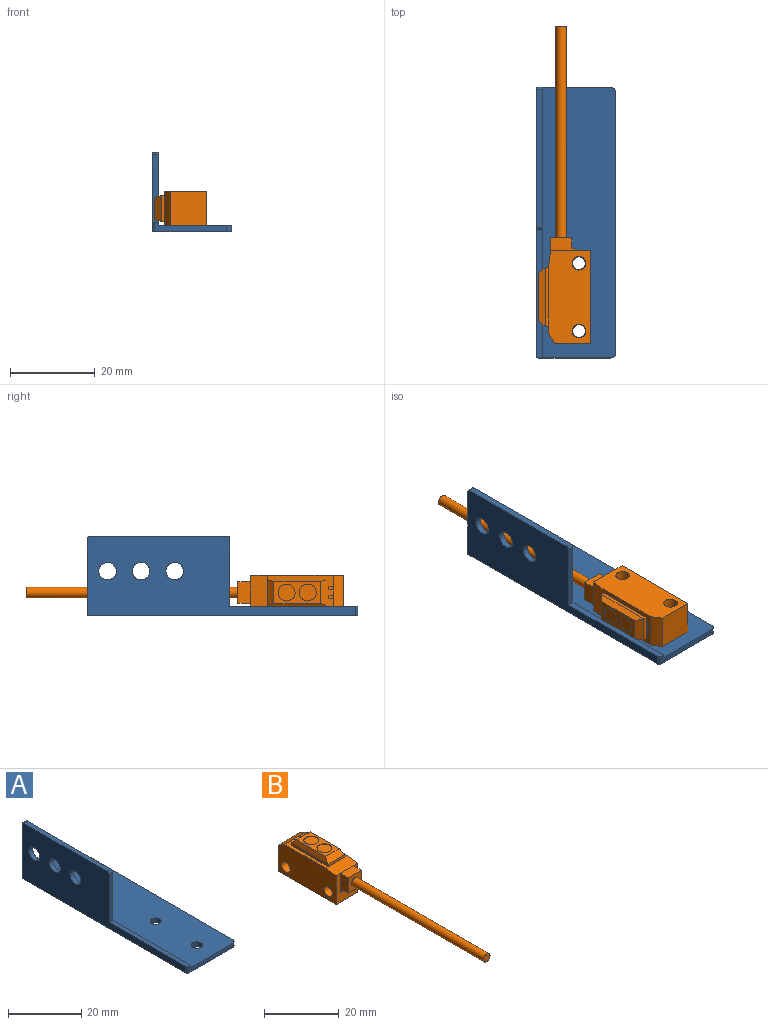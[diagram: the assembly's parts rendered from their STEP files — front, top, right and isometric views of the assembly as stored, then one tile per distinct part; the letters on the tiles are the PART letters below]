
ASSEMBLY  parts=2 mates=1
PART A: 20 faces, bbox 18.8x63.9x18.8 mm
  f0: plane 30.23x1.4mm, normal (0,0,1), area 42.1mm2, adj f3,f4,f9,f10,f16
  f1: plane 63.88x17.4mm, normal (0,0,1), area 1096.6mm2, adj f2,f4,f5,f6,f7,f9,f12,f13
  f2: plane 18.16x17.53mm, normal (0,1,0), area 47.9mm2, adj f1,f3,f8,f9,f13,f15
  f3: plane 63.25x18.8mm, normal (-1,0,0), area 655.4mm2, adj f0,f2,f8,f10,f11,f14,f15,f16
  f4: plane 16.89x2.16mm, normal (0,-1,0), area 24.2mm2, adj f0,f1,f8,f9,f12,f16
  f5: cylinder r=1.5mm len=3mm, axis (0,0,1), area 13.2mm2, adj f1,f8
  f6: plane 61.34x1.4mm, normal (1,0,0), area 85.7mm2, adj f1,f8,f12,f13
  f7: cylinder r=1.5mm len=3mm, axis (0,0,1), area 13.2mm2, adj f1,f8
  f8: plane 63.88x18.8mm, normal (0,0,-1), area 1185.8mm2, adj f2,f3,f4,f5,f6,f7,f12,f13
  f9: plane 63.88x17.4mm, normal (1,0,0), area 567.5mm2, adj f0,f1,f2,f4,f10,f11,f14,f15
  f10: plane 16x1.4mm, normal (0,-1,0), area 22.4mm2, adj f0,f3,f9,f14
  f11: plane 32.39x1.4mm, normal (0,0,1), area 45.2mm2, adj f3,f9,f14,f15
  f12: cylinder r=1.27mm len=1.4mm, axis (0,0,-1), area 2.8mm2, adj f1,f4,f6,f8
  f13: cylinder r=1.27mm len=1.4mm, axis (0,0,1), area 2.8mm2, adj f1,f2,f6,f8
  f14: cylinder r=0.64mm len=1.4mm, axis (-1,0,0), area 1.4mm2, adj f3,f9,f10,f11
  f15: cylinder r=0.64mm len=1.4mm, axis (-1,0,0), area 1.4mm2, adj f2,f3,f9,f11
  f16: cylinder r=0.64mm len=2.16mm, axis (0,0,1), area 2.2mm2, adj f0,f3,f4,f8
  f17: cylinder r=2.08mm len=4.17mm, axis (-1,0,0), area 18.3mm2, adj f3,f9
  f18: cylinder r=2.08mm len=4.17mm, axis (-1,0,0), area 18.3mm2, adj f3,f9
  f19: cylinder r=2.08mm len=4.17mm, axis (-1,0,0), area 18.3mm2, adj f3,f9
PART B: 47 faces, bbox 8.2x75x12.3 mm
  f0: cylinder r=1.25mm len=50mm, axis (0,1,0), area 392.7mm2, adj f6,f34
  f1: cylinder r=2.25mm len=4.5mm, axis (0,0,-1), area 1.4mm2, adj f16,f28
  f2: cylinder r=1.6mm len=8.2mm, axis (1,0,0), area 82.4mm2, adj f18,f20
  f3: cylinder r=1.6mm len=8.2mm, axis (1,0,0), area 82.4mm2, adj f18,f20
  f4: cylinder r=2mm len=4mm, axis (0,0,1), area 1.3mm2, adj f8,f10
  f5: cylinder r=2mm len=4mm, axis (0,0,1), area 1.3mm2, adj f8,f9
  f6: plane 5x5mm, normal (0,-1,0), area 20.1mm2, adj f0,f23,f24,f25,f27
  f7: plane 5x0.7mm, normal (0,-1,0), area 3.5mm2, adj f23,f25,f26,f27
  f8: plane 11x5.2mm, normal (0,0,1), area 32.1mm2, adj f4,f5,f35,f36,f37,f38
  f9: plane 4x4mm, normal (0,0,1), area 12.6mm2, adj f5
  f10: plane 4x4mm, normal (0,0,1), area 12.6mm2, adj f4
  f11: plane 15.5x8.2mm, normal (0,0,1), area 38.7mm2, adj f12,f13,f14,f18,f20,f21,f22,f39
  f12: plane 14x0.8mm, normal (-1,0,0), area 11.2mm2, adj f11,f13,f15,f38
  f13: plane 6.2x0.8mm, normal (0,1,0), area 5mm2, adj f11,f12,f14,f35
  f14: plane 14x0.8mm, normal (1,0,0), area 11.2mm2, adj f11,f13,f15,f37
  f15: plane 6.2x0.8mm, normal (0,-1,0), area 5mm2, adj f12,f14,f21,f36
  f16: plane 22x8.2mm, normal (0,0,-1), area 164.5mm2, adj f1,f17,f18,f19,f20
  f17: plane 9.5x8.2mm, normal (0,-1,0), area 46.9mm2, adj f16,f18,f20,f21,f23,f25,f26
  f18: plane 22x10mm, normal (1,0,0), area 201mm2, adj f2,f3,f11,f16,f17,f19,f21,f22
  f19: plane 8.5x8.2mm, normal (0,1,0), area 69.7mm2, adj f16,f18,f20,f22
  f20: plane 22x10mm, normal (-1,0,0), area 201mm2, adj f2,f3,f11,f16,f17,f19,f21,f22
  f21: plane 8.2x4mm, normal (0,-0.12,0.99), area 33.1mm2, adj f11,f15,f17,f18,f20,f24
  f22: plane 8.2x2.5mm, normal (0,0.51,0.86), area 23.6mm2, adj f11,f18,f19,f20,f39,f40,f41,f43
  f23: plane 6.2x3mm, normal (1,0,0), area 15.5mm2, adj f6,f7,f17,f24,f26,f27
  f24: plane 5x3mm, normal (0,0,1), area 15mm2, adj f6,f21,f23,f25
  f25: plane 6.2x3mm, normal (-1,0,0), area 15.5mm2, adj f6,f7,f17,f24,f26,f27
  f26: plane 5x0.5mm, normal (0,-0.71,-0.71), area 3.5mm2, adj f7,f17,f23,f25
  f27: plane 5x2.5mm, normal (0,0,-1), area 12.5mm2, adj f6,f7,f23,f25
  f28: plane 4.5x4.5mm, normal (0,0,-1), area 14.1mm2, adj f1,f29,f30,f31,f32
  f29: plane 2.12x2.12mm, normal (-0.71,0.71,0), area 0.3mm2, adj f28,f30,f32,f33
  f30: plane 0.42x0.42mm, normal (-0.71,-0.71,0), area 0.1mm2, adj f28,f29,f31,f33
  f31: plane 2.12x2.12mm, normal (0.71,-0.71,0), area 0.3mm2, adj f28,f30,f32,f33
  f32: plane 0.42x0.42mm, normal (0.71,0.71,0), area 0.1mm2, adj f28,f29,f31,f33
  f33: plane 2.55x2.55mm, normal (0,0,-1), area 1.8mm2, adj f29,f30,f31,f32
  f34: plane 2.5x2.5mm, normal (0,-1,0), area 4.9mm2, adj f0
  f35: plane 6.2x1.5mm, normal (0,0.71,0.71), area 12.1mm2, adj f8,f13,f37,f38
  f36: plane 6.2x1.5mm, normal (0,-0.71,0.71), area 12.1mm2, adj f8,f15,f37,f38
  f37: plane 14x1.5mm, normal (0.95,0,0.32), area 19.8mm2, adj f8,f14,f35,f36
  f38: plane 14x1.5mm, normal (-0.95,0,0.32), area 19.8mm2, adj f8,f12,f35,f36
  f39: plane 1.17x0.1mm, normal (1,0,0), area 0.1mm2, adj f11,f22,f41,f42
  f40: plane 1.17x0.1mm, normal (-1,0,0), area 0.1mm2, adj f11,f22,f41,f42
  f41: plane 1.17x0.8mm, normal (0,0,1), area 0.9mm2, adj f22,f39,f40,f42
  f42: plane 0.8x0.1mm, normal (0,1,0), area 0.1mm2, adj f11,f39,f40,f41
  f43: plane 1.17x0.1mm, normal (1,0,0), area 0.1mm2, adj f11,f22,f45,f46
  f44: plane 1.17x0.1mm, normal (-1,0,0), area 0.1mm2, adj f11,f22,f45,f46
  f45: plane 1.17x0.8mm, normal (0,0,1), area 0.9mm2, adj f22,f43,f44,f46
  f46: plane 0.8x0.1mm, normal (0,1,0), area 0.1mm2, adj f11,f43,f44,f45
PLACE A t=(16.11,-19.46,-18)mm
PLACE B rot(axis=(0.71,0,-0.71),180deg) t=(14.15,-15.09,-13.9)mm
MATE fastened B.f3 <-> A.f7  axis (0,0,-1) through (23.65,-25.59,-18)mm
